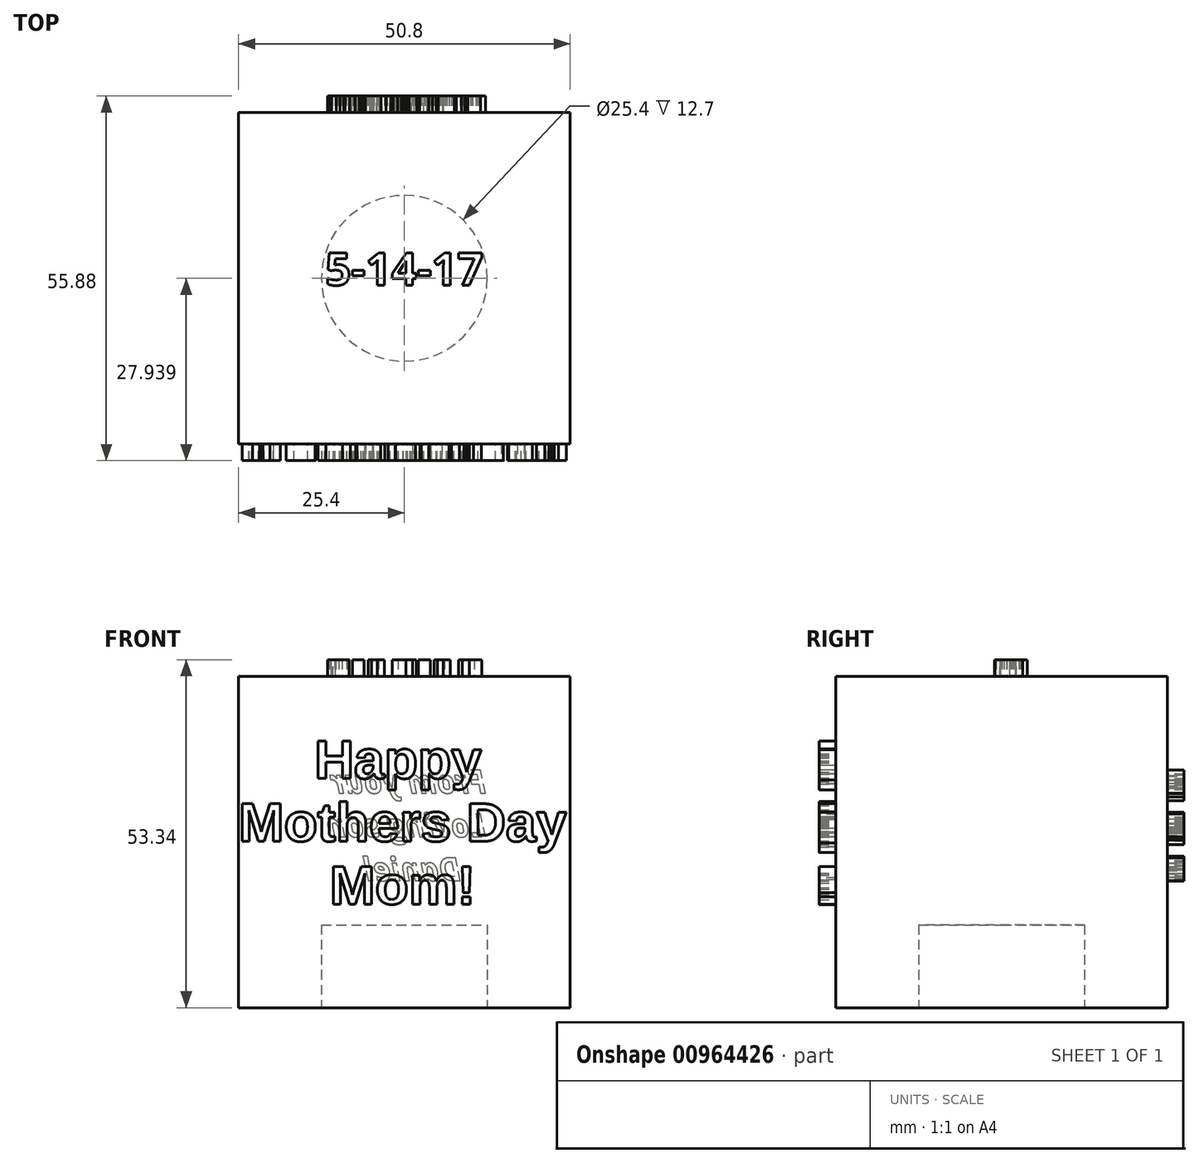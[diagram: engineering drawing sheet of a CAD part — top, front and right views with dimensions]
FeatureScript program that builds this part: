
annotation { "Feature Type Name" : "Feature", "Feature Type Description" : "" }
export const myFeature = defineFeature(function(context is Context, id is Id, definition is map)
    precondition{}
    {
        {
            var Q0;
            Q0=qCreatedBy(makeId("Top.planeOp"),FACE);
            var sketch = newSketch(context, id + "F0", { "sketchPlane" : qUnion([Q0])});
            skLineSegment(sketch, "E0.bottom", {"start": v(-147.56, -16.55) * mm, "end": v(-96.76, -16.55) * mm});
            skLineSegment(sketch, "E0.top", {"start": v(-147.56, -67.35) * mm, "end": v(-96.76, -67.35) * mm});
            skLineSegment(sketch, "E0.left", {"start": v(-147.56, -16.55) * mm, "end": v(-147.56, -67.35) * mm});
            skLineSegment(sketch, "E0.right", {"start": v(-96.76, -16.55) * mm, "end": v(-96.76, -67.35) * mm});
            skSolve(sketch);
        }
        {
            var Q0;
            Q0=makeQuery(id+"F0.imprint","IMPRINT",FACE,{"disambiguationData":[TD([[makeQuery(id+"F0.imprint","IMPRINT",EDGE,{"derivedFrom":sQuery(id+"F0.wireOp",EDGE,"E0.bottom")}),-1.0]])]});
            extrude(context, id + "F1", {"entities" : qUnion([Q0]), "depth" : 50.8 * mm, "offsetDistance" : 25.4 * mm});
        }
        {
            var Q0;
            Q0=makeQuery(id+"F1.opExtrude","SWEPT_FACE",FACE,{"disambiguationData":[OSD([sQuery(id+"F0.wireOp",EDGE,"E0.top")])]});
            var sketch = newSketch(context, id + "F2", { "sketchPlane" : qUnion([Q0])});
            skText(sketch, "E1", { "text": "     \n     Happy\nMothers Day\n      Mom!", "fontName": "Arimo-Bold.ttf"});
            skPoint(sketch, "E2", {"position": v(-96.76, 25.4) * mm});
            const initialGuessF2  = {"E1": [-0.14756, 0.04477, 1, 0, 0.00603]};
            skSetInitialGuess(sketch, initialGuessF2);
            skSolve(sketch);
        }
        {
            var Q0;
            Q0=qSketchRegion(id+"F2",true);
            extrude(context, id + "F3", {"entities" : qUnion([Q0]), "operationType" : NewBodyOperationType.ADD, "depth" : 2.54 * mm, "offsetDistance" : 25.4 * mm});
        }
        {
            var Q0;
            Q0=makeQuery(id+"F1.opExtrude","CAP_FACE",FACE,{"disambiguationData":[OSD([sQuery(id+"F0.wireOp",EDGE,"E0.bottom"),sQuery(id+"F0.wireOp",EDGE,"E0.top"),sQuery(id+"F0.wireOp",EDGE,"E0.left"),sQuery(id+"F0.wireOp",EDGE,"E0.right")])],"isStart":false});
            var sketch = newSketch(context, id + "F4", { "sketchPlane" : qUnion([Q0])});
            skText(sketch, "E3", { "text": "5-14-17", "fontName": "OpenSans-Bold.ttf"});
            const initialGuessF4  = {"E3": [-0.13428, -0.043, 1, 0, 0.00498]};
            skSetInitialGuess(sketch, initialGuessF4);
            skSolve(sketch);
        }
        {
            var Q0;
            Q0 = qSketchRegion(id + "F4", true);
            extrude(context, id + "F5", {"entities" : qUnion([Q0]), "operationType" : NewBodyOperationType.ADD, "depth" : 2.54 * mm, "offsetDistance" : 25.4 * mm});
        }
        {
            var Q0;
            Q0=makeQuery(id+"F1.opExtrude","SWEPT_FACE",FACE,{"disambiguationData":[OSD([sQuery(id+"F0.wireOp",EDGE,"E0.bottom")])]});
            var sketch = newSketch(context, id + "F6", { "sketchPlane" : qUnion([Q0])});
            skText(sketch, "E4", { "text": "From your\nLoving son\n   Daniel", "fontName": "OpenSans-BoldItalic.ttf"});
            const initialGuessF6  = {"E4": [0.10961, 0.03288, 1, 0, 0.00355]};
            skSetInitialGuess(sketch, initialGuessF6);
            skSolve(sketch);
        }
        {
            var Q0;
            Q0 = qSketchRegion(id + "F6", true);
            extrude(context, id + "F7", {"entities" : qUnion([Q0]), "operationType" : NewBodyOperationType.ADD, "depth" : 2.54 * mm, "offsetDistance" : 25.4 * mm});
        }
        {
            var Q0;
            Q0=makeQuery(id+"F1.opExtrude","CAP_FACE",FACE,{"disambiguationData":[OSD([sQuery(id+"F0.wireOp",EDGE,"E0.bottom"),sQuery(id+"F0.wireOp",EDGE,"E0.top"),sQuery(id+"F0.wireOp",EDGE,"E0.left"),sQuery(id+"F0.wireOp",EDGE,"E0.right")])],"isStart":true});
            var sketch = newSketch(context, id + "F8", { "sketchPlane" : qUnion([Q0])});
            skCircle(sketch, "E5", {"center": v(-122.16, 41.95) * mm, "radius": 12.7 * mm});
            skSolve(sketch);
        }
        {
            var Q0;
            Q0 = qSketchRegion(id + "F8", true);
            extrude(context, id + "F9", {"entities" : qUnion([Q0]), "operationType" : NewBodyOperationType.REMOVE, "oppositeDirection" : true, "depth" : 12.7 * mm, "offsetDistance" : 25.4 * mm});
        }
    });
